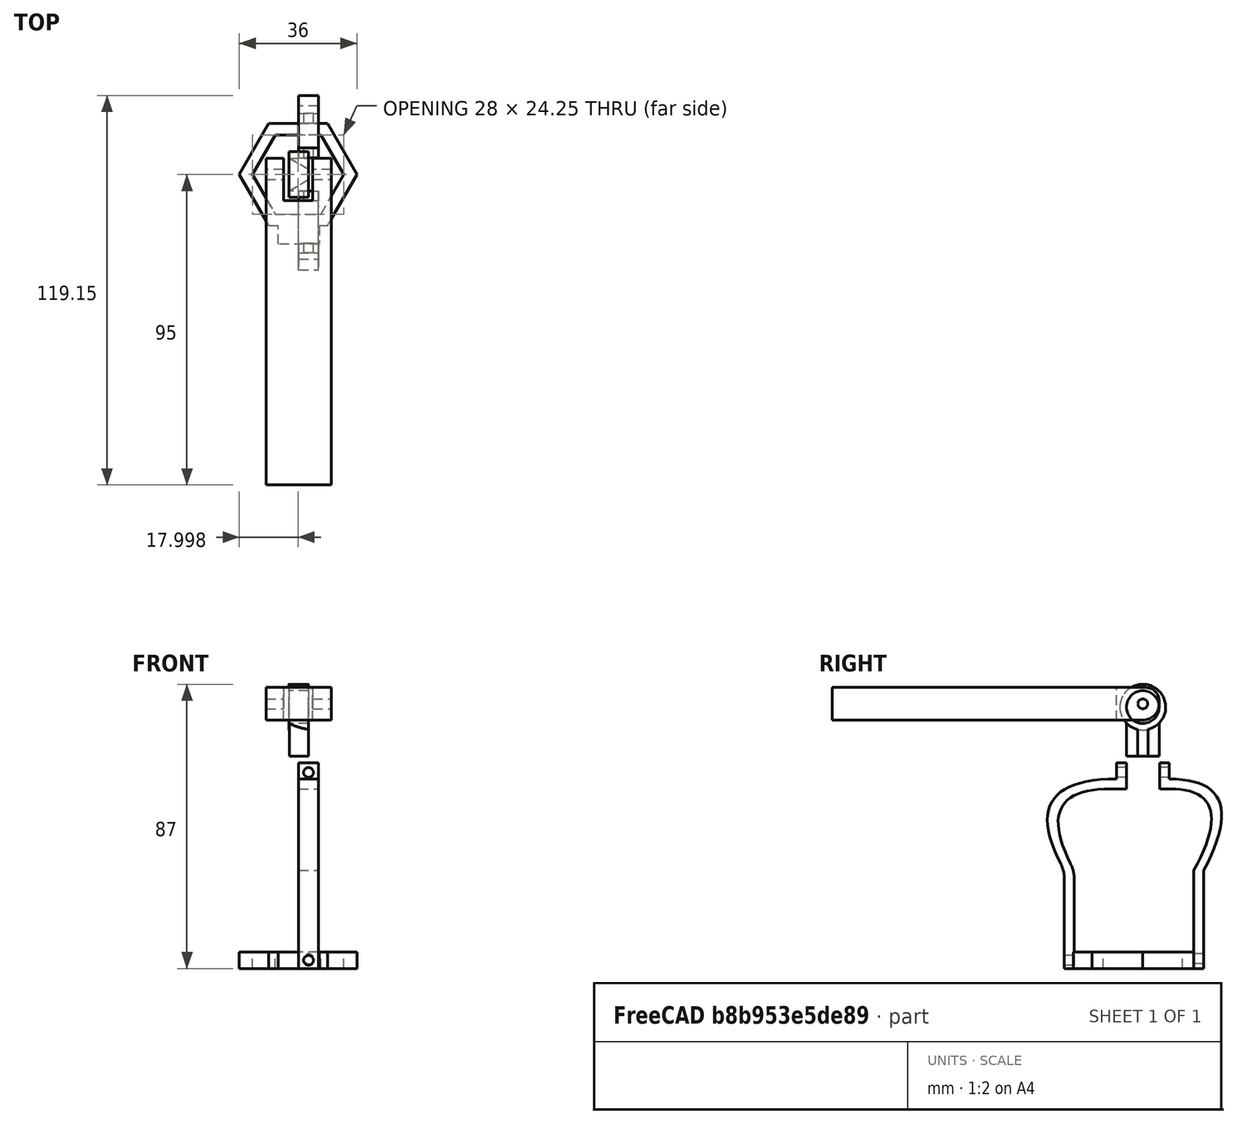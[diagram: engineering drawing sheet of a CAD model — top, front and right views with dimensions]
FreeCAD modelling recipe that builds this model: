
FCSTD DOCUMENT  (FreeCAD 0.20R29177 +426 (Git))
Label: june_support
License: All rights reserved
LicenseURL: http://en.wikipedia.org/wiki/All_rights_reserved
objects: Sketcher::SketchObject×12, PartDesign::Pad×7, PartDesign::Fillet×6, PartDesign::Body×5, PartDesign::Pocket×5, Mesh::Feature×1
note: 53 computed .brp shape members not serialized (recipe doc carries the construction recipe); baked Part::Feature solids carry a one-line shape summary decoded from their .brp

FEATURE [Mesh::Feature] GripperHexBase
  Placement = pos=(0,1,4) rot=(0,0,1;1.0472rad)
FEATURE [Sketcher::SketchObject] Sketch
  FullyConstrained = false
  MapMode = 5
  Support = -> [XY_Plane]
  sketch-geometry (14):
    g0: LineSegment StartX=17.8182 StartY=0 StartZ=0 EndX=8.81825 EndY=15.5885 EndZ=0
    g1: LineSegment StartX=8.81825 StartY=15.5885 StartZ=0 EndX=-9.18175 EndY=15.5885 EndZ=0
    g2: LineSegment StartX=-9.18175 StartY=15.5885 StartZ=0 EndX=-18.1818 EndY=1.10454e-11 EndZ=0
    g3: LineSegment StartX=-18.1818 StartY=1.10451e-11 StartZ=0 EndX=-9.18175 EndY=-15.5885 EndZ=0
    g4: LineSegment StartX=-9.18175 StartY=-15.5885 StartZ=0 EndX=8.81825 EndY=-15.5885 EndZ=0
    g5: LineSegment StartX=8.81825 StartY=-15.5885 StartZ=0 EndX=17.8182 EndY=0 EndZ=0
    g6: Circle CenterX=-0.181751 CenterY=0 CenterZ=0 NormalX=0 NormalY=0 NormalZ=1 AngleXU=0 Radius=18
    g7: LineSegment StartX=-14.1818 StartY=0 StartZ=0 EndX=-7.18175 EndY=-12.1244 EndZ=0
    g8: LineSegment StartX=-7.18175 StartY=-12.1244 StartZ=0 EndX=6.81825 EndY=-12.1244 EndZ=0
    g9: LineSegment StartX=6.81825 StartY=-12.1244 StartZ=0 EndX=13.8182 EndY=9.5568e-12 EndZ=0
    g10: LineSegment StartX=13.8182 StartY=9.5568e-12 StartZ=0 EndX=6.81825 EndY=12.1244 EndZ=0
    g11: LineSegment StartX=6.81825 StartY=12.1244 StartZ=0 EndX=-7.18175 EndY=12.1244 EndZ=0
    g12: LineSegment StartX=-7.18175 StartY=12.1244 StartZ=0 EndX=-14.1818 EndY=0 EndZ=0
    g13: Circle CenterX=-0.181751 CenterY=0 CenterZ=0 NormalX=0 NormalY=0 NormalZ=1 AngleXU=0 Radius=14
  constraints (32):
    c: Coincident(g0,g1)
    c: Coincident(g1,g2)
    c: Coincident(g2,g3)
    c: Coincident(g3,g4)
    c: Coincident(g4,g5)
    c: Coincident(g5,g0)
    c: Equal(g0, g1-g5) x5
    c: PointOnObject(g0,g6)
    c: PointOnObject(g1,g6)
    c: PointOnObject(g2,g6)
    c: PointOnObject(g3,g6)
    c: PointOnObject(g4,g6)
    c: PointOnObject(g5,g6)
    c: PointOnObject(g6,g-1)
    c: PointOnObject(g5,g-1)
    c: Radius(g6) = 18
    c: Coincident(g7,g8)
    c: Coincident(g8,g9)
    c: Coincident(g9,g10)
    c: Coincident(g10,g11)
    c: Coincident(g11,g12)
    c: Coincident(g12,g7)
    c: Equal(g7, g8-g12) x5
    c: PointOnObject(g7,g13)
    c: PointOnObject(g8,g13)
    c: PointOnObject(g9,g13)
    c: PointOnObject(g10,g13)
    c: PointOnObject(g11,g13)
    c: PointOnObject(g12,g13)
    c: Coincident(g13,g6)
    c: PointOnObject(g12,g-1)
    c: Radius(g13) = 14
FEATURE [PartDesign::Pad] Pad
  Direction = (0,0,1)
  Length = 5
  Length2 = 10
  Profile = -> Sketch
  ReferenceAxis = -> Sketch [N_Axis]
  Type = 0
FEATURE [Sketcher::SketchObject] Sketch001
  FullyConstrained = true
  MapMode = 5
  Support = -> [XY_Plane]
  sketch-geometry (4):
    g0: LineSegment StartX=-6.25 StartY=-15.5 StartZ=0 EndX=6.25 EndY=-15.5 EndZ=0
    g1: LineSegment StartX=6.25 StartY=-15.5 StartZ=0 EndX=6.25 EndY=-21.3 EndZ=0
    g2: LineSegment StartX=6.25 StartY=-21.3 StartZ=0 EndX=-6.25 EndY=-21.3 EndZ=0
    g3: LineSegment StartX=-6.25 StartY=-21.3 StartZ=0 EndX=-6.25 EndY=-15.5 EndZ=0
  constraints (11):
    c: Coincident(g0,g1)
    c: Coincident(g1,g2)
    c: Coincident(g2,g3)
    c: Coincident(g3,g0)
    c: Horizontal(g2)
    c: Vertical(g1)
    c: Vertical(g3)
    c: DistanceX(g0,g0) = 12.5
    c: DistanceY(g0,g-1) = 15.5
    c: Symmetric(g0,g0,g-2)
    c: DistanceY(g1,g1) = 5.8
FEATURE [PartDesign::Pad] Pad001
  BaseFeature = -> Pad
  Direction = (0,0,1)
  Length = 5
  Length2 = 10
  Profile = -> Sketch001
  ReferenceAxis = -> Sketch001 [N_Axis]
  Type = 0
FEATURE [PartDesign::Body] Body
  Group = -> [Sketch,Pad,Sketch001,Pad001]
  Origin = -> Origin
  Tip = -> Pad001
FEATURE [Sketcher::SketchObject] Sketch002
  FullyConstrained = false
  MapMode = 5
  Placement = pos=(0,0,0) rot=(0.57735,0.57735,0.57735;2.0944rad)
  Support = -> [YZ_Plane001]
  sketch-geometry (20):
    g0: LineSegment StartX=-21 StartY=0 StartZ=0 EndX=-21 EndY=30 EndZ=0
    g1: LineSegment StartX=-24 StartY=30 StartZ=0 EndX=-24 EndY=0 EndZ=0
    g2: LineSegment StartX=-24 StartY=0 StartZ=0 EndX=-21 EndY=0 EndZ=0
    g3: LineSegment StartX=-8 StartY=63 StartZ=0 EndX=-5 EndY=63 EndZ=0
    g4: LineSegment StartX=-5 StartY=63 StartZ=0 EndX=-5 EndY=55 EndZ=0
    g5: LineSegment StartX=-5 StartY=55 StartZ=0 EndX=-9.87767 EndY=55 EndZ=0
    g6: GeomPoint X=-8 Y=58 Z=0
    g7: Circle CenterX=-21 CenterY=30 CenterZ=0 NormalX=0 NormalY=0 NormalZ=1 AngleXU=0 Radius=1
    g8: Circle CenterX=-34.7506 CenterY=55 CenterZ=0 NormalX=0 NormalY=0 NormalZ=1 AngleXU=0 Radius=1
    g9: Circle CenterX=-9.87767 CenterY=55 CenterZ=0 NormalX=0 NormalY=0 NormalZ=1 AngleXU=0 Radius=1
    g10: BSplineCurve PolesCount=3 KnotsCount=2 Degree=2 IsPeriodic=0
    g11: GeomPoint X=-21 Y=30 Z=0
    g12: GeomPoint X=-9.87767 Y=55 Z=0
    g13: Circle CenterX=-24 CenterY=30 CenterZ=0 NormalX=0 NormalY=0 NormalZ=1 AngleXU=0 Radius=1
    g14: Circle CenterX=-39.6851 CenterY=58 CenterZ=0 NormalX=0 NormalY=0 NormalZ=1 AngleXU=0 Radius=1
    g15: Circle CenterX=-8 CenterY=58 CenterZ=0 NormalX=0 NormalY=0 NormalZ=1 AngleXU=0 Radius=1
    g16: BSplineCurve PolesCount=3 KnotsCount=2 Degree=2 IsPeriodic=0
    g17: GeomPoint X=-24 Y=30 Z=0
    g18: GeomPoint X=-8 Y=58 Z=0
    g19: LineSegment StartX=-8 StartY=58 StartZ=0 EndX=-8 EndY=63 EndZ=0
  constraints (43):
    c: PointOnObject(g0,g-1)
    c: Vertical(g0)
    c: PointOnObject(g1,g-1)
    c: Vertical(g1)
    c: Coincident(g1,g2)
    c: Coincident(g2,g0)
    c: DistanceY(g0,g0) = 30
    c: DistanceX(g1,g0) = 3
    c: DistanceX(g0,g-1) = 21
    c: Coincident(g3,g4)
    c: Coincident(g4,g5)
    c: Coincident(g19,g3)
    c: Horizontal(g3)
    c: Horizontal(g5)
    c: Vertical(g4)
    c: DistanceY(g4,g4) = 8
    c: DistanceX(g3,g3) = 3
    c: DistanceY(g5,g6) = 3
    c: DistanceY(g-1,g4) = 55
    c: Weight(g7) = 1
    c: Coincident(g10,g0)
    c: Equal(g7,g8)
    c: Equal(g7,g9)
    c: Coincident(g10,g5)
    c: InternalAlignment(g7,g10)
    c: InternalAlignment(g8,g10)
    c: InternalAlignment(g9,g10)
    c: InternalAlignment(g11,g10)
    c: InternalAlignment(g12,g10)
    c: DistanceY(g-1,g8) = 55
    c: Weight(g13) = 1
    c: Equal(g13,g14)
    c: Equal(g13,g15)
    c: Coincident(g16,g6)
    c: InternalAlignment(g13,g16)
    c: InternalAlignment(g14,g16)
    c: InternalAlignment(g15,g16)
    c: InternalAlignment(g17,g16)
    c: InternalAlignment(g18,g16)
    c: DistanceY(g-1,g14) = 58
    c: Coincident(g19,g16)
    c: DistanceX(g4,g-1) = 5
    c: Vertical(g19)
FEATURE [PartDesign::Pad] Pad002
  Direction = (1,-2e-16,3e-16)
  Length = 6
  Length2 = 10
  Placement = pos=(0,0,0) rot=(0.57735,0.57735,0.57735;2.0944rad)
  Profile = -> Sketch002
  ReferenceAxis = -> Sketch002 [N_Axis]
  Type = 0
FEATURE [PartDesign::Fillet] Fillet
  Base = -> Pad002 [Edge1]
  BaseFeature = -> Pad002
  Placement = pos=(0,0,0) rot=(0.57735,0.57735,0.57735;2.0944rad)
  Radius = 10
  SupportTransform = false
  UseAllEdges = false
FEATURE [PartDesign::Fillet] Fillet001
  Base = -> Fillet [Edge26]
  BaseFeature = -> Fillet
  Placement = pos=(0,0,0) rot=(0.57735,0.57735,0.57735;2.0944rad)
  Radius = 10
  SupportTransform = false
  UseAllEdges = false
FEATURE [Sketcher::SketchObject] Sketch003
  FullyConstrained = true
  MapMode = 5
  Placement = pos=(0,0,0) rot=(1,0,0;1.5708rad)
  Support = -> [XZ_Plane001]
  sketch-geometry (2):
    g0: Circle CenterX=3 CenterY=60 CenterZ=0 NormalX=0 NormalY=0 NormalZ=1 AngleXU=0 Radius=1.5
    g1: Circle CenterX=3 CenterY=2.5 CenterZ=0 NormalX=0 NormalY=0 NormalZ=1 AngleXU=0 Radius=1.5
  constraints (6):
    c: Radius(g0) = 1.5
    c: Radius(g1) = 1.5
    c: DistanceX(g-1,g0) = 3
    c: DistanceX(g-1,g1) = 3
    c: DistanceY(g-1,g1) = 2.5
    c: DistanceY(g-1,g0) = 60
FEATURE [PartDesign::Pocket] Pocket
  BaseFeature = -> Fillet001
  Direction = (0,1,-2e-16)
  Length = 5
  Length2 = 5
  Midplane = true
  Placement = pos=(0,0,0) rot=(0.57735,0.57735,0.57735;2.0944rad)
  Profile = -> Sketch003
  ReferenceAxis = -> Sketch003 [N_Axis]
  Type = 1
FEATURE [PartDesign::Body] Body001  label="servo_side_support"
  Group = -> [Sketch002,Pad002,Fillet,Fillet001,Sketch003,Pocket]
  Origin = -> Origin001
  Tip = -> Pocket
FEATURE [Sketcher::SketchObject] Sketch004
  FullyConstrained = false
  MapMode = 5
  Placement = pos=(0,0,0) rot=(0.57735,0.57735,0.57735;2.0944rad)
  Support = -> [YZ_Plane002]
  sketch-geometry (20):
    g0: GeomPoint X=15.6357 Y=0 Z=0
    g1: LineSegment StartX=15.6357 StartY=0 StartZ=0 EndX=18.6357 EndY=0 EndZ=0
    g2: LineSegment StartX=18.6357 StartY=0 StartZ=0 EndX=18.6357 EndY=30 EndZ=0
    g3: LineSegment StartX=15.6357 StartY=30 StartZ=0 EndX=15.6357 EndY=0 EndZ=0
    g4: LineSegment StartX=5.15555 StartY=63 StartZ=0 EndX=8.15555 EndY=63 EndZ=0
    g5: LineSegment StartX=8.15555 StartY=63 StartZ=0 EndX=8.15555 EndY=58 EndZ=0
    g6: LineSegment StartX=8.15555 StartY=55 StartZ=0 EndX=5.15555 EndY=55 EndZ=0
    g7: LineSegment StartX=5.15555 StartY=55 StartZ=0 EndX=5.15555 EndY=63 EndZ=0
    g8: Circle CenterX=15.6357 CenterY=30 CenterZ=0 NormalX=0 NormalY=0 NormalZ=1 AngleXU=0 Radius=1
    g9: Circle CenterX=29.3875 CenterY=55 CenterZ=0 NormalX=0 NormalY=0 NormalZ=1 AngleXU=0 Radius=1
    g10: Circle CenterX=8.15555 CenterY=55 CenterZ=0 NormalX=0 NormalY=0 NormalZ=1 AngleXU=0 Radius=1
    g11: BSplineCurve PolesCount=3 KnotsCount=2 Degree=2 IsPeriodic=0
    g12: GeomPoint X=15.6357 Y=30 Z=0
    g13: GeomPoint X=8.15555 Y=55 Z=0
    g14: Circle CenterX=18.6357 CenterY=30 CenterZ=0 NormalX=0 NormalY=0 NormalZ=1 AngleXU=0 Radius=1
    g15: Circle CenterX=33.5466 CenterY=58 CenterZ=0 NormalX=0 NormalY=0 NormalZ=1 AngleXU=0 Radius=1
    g16: Circle CenterX=8.15555 CenterY=58 CenterZ=0 NormalX=0 NormalY=0 NormalZ=1 AngleXU=0 Radius=1
    g17: BSplineCurve PolesCount=3 KnotsCount=2 Degree=2 IsPeriodic=0
    g18: GeomPoint X=18.6357 Y=30 Z=0
    g19: GeomPoint X=8.15555 Y=58 Z=0
  constraints (41):
    c: PointOnObject(g0,g-1)
    c: Coincident(g1,g0)
    c: PointOnObject(g1,g-1)
    c: Coincident(g1,g2)
    c: Vertical(g2)
    c: Coincident(g3,g1)
    c: Vertical(g3)
    c: DistanceX(g1,g1) = 3
    c: DistanceY(g2,g2) = 30
    c: Coincident(g4,g5)
    c: Coincident(g6,g7)
    c: Coincident(g7,g4)
    c: Horizontal(g4)
    c: Horizontal(g6)
    c: Vertical(g5)
    c: Vertical(g7)
    c: DistanceY(g7,g7) = 8
    c: DistanceX(g4,g4) = 3
    c: Weight(g8) = 1
    c: Equal(g8,g9)
    c: Equal(g8,g10)
    c: Coincident(g11,g6)
    c: InternalAlignment(g8,g11)
    c: InternalAlignment(g9,g11)
    c: InternalAlignment(g10,g11)
    c: InternalAlignment(g12,g11)
    c: InternalAlignment(g13,g11)
    c: Weight(g14) = 1
    c: Coincident(g17,g2)
    c: Equal(g14,g15)
    c: Equal(g14,g16)
    c: InternalAlignment(g14,g17)
    c: InternalAlignment(g15,g17)
    c: InternalAlignment(g16,g17)
    c: InternalAlignment(g18,g17)
    c: InternalAlignment(g19,g17)
    c: Coincident(g5,g17)
    c: DistanceY(g5,g5) = 5
    c: DistanceY(g-1,g6) = 55
    c: DistanceY(g-1,g9) = 55
    c: DistanceY(g-1,g15) = 58
FEATURE [PartDesign::Pad] Pad003
  Direction = (1,-2e-16,3e-16)
  Length = 6
  Length2 = 10
  Placement = pos=(0,0,0) rot=(0.57735,0.57735,0.57735;2.0944rad)
  Profile = -> Sketch004
  ReferenceAxis = -> Sketch004 [N_Axis]
  Type = 0
FEATURE [Sketcher::SketchObject] Sketch005
  FullyConstrained = true
  MapMode = 5
  Placement = pos=(0,0,0) rot=(1,0,0;1.5708rad)
  Support = -> [XZ_Plane002]
  sketch-geometry (2):
    g0: Circle CenterX=3 CenterY=3 CenterZ=0 NormalX=0 NormalY=0 NormalZ=1 AngleXU=0 Radius=1.5
    g1: Circle CenterX=3 CenterY=60 CenterZ=0 NormalX=0 NormalY=0 NormalZ=1 AngleXU=0 Radius=1.5
  constraints (6):
    c: Radius(g0) = 1.5
    c: DistanceY(g-1,g0) = 3
    c: DistanceX(g-1,g0) = 3
    c: Radius(g1) = 1.5
    c: DistanceX(g-1,g1) = 3
    c: DistanceY(g-1,g1) = 60
FEATURE [PartDesign::Pocket] Pocket001
  BaseFeature = -> Pad003
  Direction = (0,1,-2e-16)
  Length = 5
  Length2 = 5
  Placement = pos=(0,0,0) rot=(0.57735,0.57735,0.57735;2.0944rad)
  Profile = -> Sketch005
  ReferenceAxis = -> Sketch005 [N_Axis]
  Type = 1
FEATURE [PartDesign::Body] Body002  label="servo_side_support_same"
  Group = -> [Sketch004,Pad003,Sketch005,Pocket001]
  Origin = -> Origin002
  Tip = -> Pocket001
FEATURE [Sketcher::SketchObject] Sketch006
  FullyConstrained = true
  MapMode = 5
  Support = -> [XY_Plane003]
  sketch-geometry (4):
    g0: LineSegment StartX=5.7735 StartY=0 StartZ=0 EndX=-2.88675 EndY=5 EndZ=0
    g1: LineSegment StartX=-2.88675 StartY=5 StartZ=0 EndX=-2.88675 EndY=-5 EndZ=0
    g2: LineSegment StartX=-2.88675 StartY=-5 StartZ=0 EndX=5.7735 EndY=0 EndZ=0
    g3: Circle CenterX=0 CenterY=0 CenterZ=0 NormalX=0 NormalY=0 NormalZ=1 AngleXU=0 Radius=5.7735
  constraints (11):
    c: Coincident(g0,g1)
    c: Coincident(g1,g2)
    c: Coincident(g2,g0)
    c: Equal(g0,g1)
    c: Equal(g0,g2)
    c: PointOnObject(g0,g3)
    c: PointOnObject(g1,g3)
    c: PointOnObject(g2,g3)
    c: Coincident(g3,g-1)
    c: PointOnObject(g2,g-1)
    c: Distance(g0) = 10
FEATURE [PartDesign::Pad] Pad004
  Direction = (0,0,1)
  Length = 10
  Length2 = 10
  Profile = -> Sketch006
  ReferenceAxis = -> Sketch006 [N_Axis]
  Type = 0
FEATURE [Sketcher::SketchObject] Sketch007
  ExternalGeometry = -> [Pad004]
  FullyConstrained = true
  MapMode = 5
  Placement = pos=(0,0,0) rot=(0.57735,0.57735,0.57735;2.0944rad)
  Support = -> [YZ_Plane003]
  sketch-geometry (2):
    g0: Circle CenterX=0 CenterY=15 CenterZ=0 NormalX=0 NormalY=0 NormalZ=1 AngleXU=0 Radius=7
    g1: Circle CenterX=0 CenterY=15 CenterZ=0 NormalX=0 NormalY=0 NormalZ=1 AngleXU=0 Radius=5
  constraints (5):
    c: PointOnObject(g0,g-2)
    c: Radius(g0) = 7
    c: Coincident(g1,g0)
    c: Radius(g1) = 5
    c: DistanceY(g-3,g0) = 5
FEATURE [PartDesign::Pad] Pad005
  BaseFeature = -> Pad004
  Direction = (1,-2e-16,3e-16)
  Length = 6
  Length2 = 10
  Midplane = true
  Profile = -> Sketch007
  ReferenceAxis = -> Sketch007 [N_Axis]
  Type = 0
FEATURE [Sketcher::SketchObject] Sketch008
  AttachmentOffset = pos=(0,0,81) rot=(0,0,1;0rad)
  FullyConstrained = false
  MapMode = 5
  Placement = pos=(0,0,81) rot=(0,0,1;0rad)
  Support = -> [XY_Plane004]
  sketch-geometry (4):
    g0: LineSegment StartX=-10 StartY=5 StartZ=0 EndX=10 EndY=5 EndZ=0
    g1: LineSegment StartX=10 StartY=5 StartZ=0 EndX=10 EndY=-95 EndZ=0
    g2: LineSegment StartX=10 StartY=-95 StartZ=0 EndX=-10 EndY=-95 EndZ=0
    g3: LineSegment StartX=-10 StartY=-95 StartZ=0 EndX=-10 EndY=5 EndZ=0
  constraints (11):
    c: Coincident(g0,g1)
    c: Coincident(g1,g2)
    c: Coincident(g2,g3)
    c: Coincident(g3,g0)
    c: Horizontal(g2)
    c: Vertical(g1)
    c: Vertical(g3)
    c: DistanceX(g2,g2) = 20
    c: DistanceY(g3,g3) = 100
    c: DistanceX(g0,g-1) = 10
    c: DistanceY(g-1,g0) = 5
FEATURE [PartDesign::Pad] Pad006
  Direction = (0,0,1)
  Length = 10
  Length2 = 10
  Midplane = true
  Profile = -> Sketch008
  ReferenceAxis = -> Sketch008 [N_Axis]
  Type = 0
FEATURE [Sketcher::SketchObject] Sketch009
  FullyConstrained = false
  MapMode = 5
  Support = -> [XY_Plane004]
  sketch-geometry (4):
    g0: LineSegment StartX=-4.67524 StartY=5 StartZ=0 EndX=4.32476 EndY=5 EndZ=0
    g1: LineSegment StartX=4.32476 StartY=5 StartZ=0 EndX=4.32476 EndY=-8 EndZ=0
    g2: LineSegment StartX=4.32476 StartY=-8 StartZ=0 EndX=-4.67524 EndY=-8 EndZ=0
    g3: LineSegment StartX=-4.67524 StartY=-8 StartZ=0 EndX=-4.67524 EndY=5 EndZ=0
  constraints (11):
    c: Coincident(g0,g1)
    c: Coincident(g1,g2)
    c: Coincident(g2,g3)
    c: Coincident(g3,g0)
    c: Horizontal(g0)
    c: Horizontal(g2)
    c: Vertical(g1)
    c: Vertical(g3)
    c: DistanceX(g0,g0) = 9
    c: DistanceY(g1,g1) = 13
    c: DistanceY(g2,g-1) = 8
FEATURE [PartDesign::Pocket] Pocket002
  BaseFeature = -> Pad006
  Direction = (0,0,-1)
  Length = 5
  Length2 = 5
  Profile = -> Sketch009
  ReferenceAxis = -> Sketch009 [N_Axis]
  Reversed = true
  Type = 1
FEATURE [Sketcher::SketchObject] Sketch010
  ExternalGeometry = -> [Pocket002]
  FullyConstrained = true
  MapMode = 5
  Placement = pos=(0,0,0) rot=(0.57735,0.57735,0.57735;2.0944rad)
  Support = -> [YZ_Plane004]
  sketch-geometry (1):
    g0: Circle CenterX=0 CenterY=81 CenterZ=0 NormalX=0 NormalY=0 NormalZ=1 AngleXU=0 Radius=1.5
  constraints (3):
    c: Radius(g0) = 1.5
    c: DistanceX(g0,g-1) = 0
    c: DistanceY(g0) = 81
FEATURE [PartDesign::Pocket] Pocket003
  BaseFeature = -> Pocket002
  Direction = (-1,2e-16,-3e-16)
  Length = 5
  Length2 = 5
  Midplane = true
  Profile = -> Sketch010
  ReferenceAxis = -> Sketch010 [N_Axis]
  Type = 1
FEATURE [PartDesign::Fillet] Fillet002
  Base = -> Pocket003 [Edge8]
  BaseFeature = -> Pocket003
  Radius = 5
  SupportTransform = false
  UseAllEdges = false
FEATURE [PartDesign::Fillet] Fillet003
  Base = -> Fillet002 [Edge7]
  BaseFeature = -> Fillet002
  Radius = 5
  SupportTransform = false
  UseAllEdges = false
FEATURE [PartDesign::Fillet] Fillet004
  Base = -> Fillet003 [Edge34]
  BaseFeature = -> Fillet003
  Radius = 4
  SupportTransform = false
  UseAllEdges = false
FEATURE [PartDesign::Fillet] Fillet005
  Base = -> Fillet004 [Edge19]
  BaseFeature = -> Fillet004
  Radius = 4
  SupportTransform = false
  UseAllEdges = false
FEATURE [PartDesign::Body] Body004  label="arm"
  Group = -> [Sketch008,Pad006,Sketch009,Pocket002,Sketch010,Pocket003,Fillet002,Fillet003,Fillet004,Fillet005]
  Origin = -> Origin004
  Tip = -> Fillet005
FEATURE [Sketcher::SketchObject] Sketch011
  FullyConstrained = false
  MapMode = 5
  Support = -> [XY_Plane003]
  sketch-geometry (8):
    g0: LineSegment StartX=-3 StartY=7 StartZ=0 EndX=3 EndY=7 EndZ=0
    g1: LineSegment StartX=3 StartY=7 StartZ=0 EndX=3 EndY=-7 EndZ=0
    g2: LineSegment StartX=3 StartY=-7 StartZ=0 EndX=-3 EndY=-7 EndZ=0
    g3: LineSegment StartX=-3 StartY=-7 StartZ=0 EndX=-3 EndY=7 EndZ=0
    g4: LineSegment StartX=-5.93206 StartY=9.45748 StartZ=0 EndX=6.15942 EndY=9.45748 EndZ=0
    g5: LineSegment StartX=6.15942 StartY=9.45748 StartZ=0 EndX=6.15942 EndY=-9.05943 EndZ=0
    g6: LineSegment StartX=6.15942 StartY=-9.05943 StartZ=0 EndX=-5.93206 EndY=-9.05943 EndZ=0
    g7: LineSegment StartX=-5.93206 StartY=-9.05943 StartZ=0 EndX=-5.93206 EndY=9.45748 EndZ=0
  constraints (19):
    c: Coincident(g0,g1)
    c: Coincident(g1,g2)
    c: Coincident(g2,g3)
    c: Coincident(g3,g0)
    c: Horizontal(g0)
    c: Horizontal(g2)
    c: Vertical(g1)
    c: Vertical(g3)
    c: Coincident(g4,g5)
    c: Coincident(g5,g6)
    c: Coincident(g6,g7)
    c: Coincident(g7,g4)
    c: Horizontal(g4)
    c: Horizontal(g6)
    c: Vertical(g5)
    c: Vertical(g7)
    c: Symmetric(g0,g1,g-1)
    c: DistanceX(g0,g0) = 6
    c: DistanceY(g1,g1) = 14
FEATURE [PartDesign::Pocket] Pocket004
  BaseFeature = -> Pad005
  Direction = (0,0,-1)
  Length = 5
  Length2 = 5
  Profile = -> Sketch011
  ReferenceAxis = -> Sketch011 [N_Axis]
  Reversed = true
  Type = 1
FEATURE [PartDesign::Body] Body003  label="top holder"
  Group = -> [Sketch006,Pad004,Sketch007,Pad005,Sketch011,Pocket004]
  Origin = -> Origin003
  Placement = pos=(0,0,65) rot=(0,0,1;0rad)
  Tip = -> Pocket004
